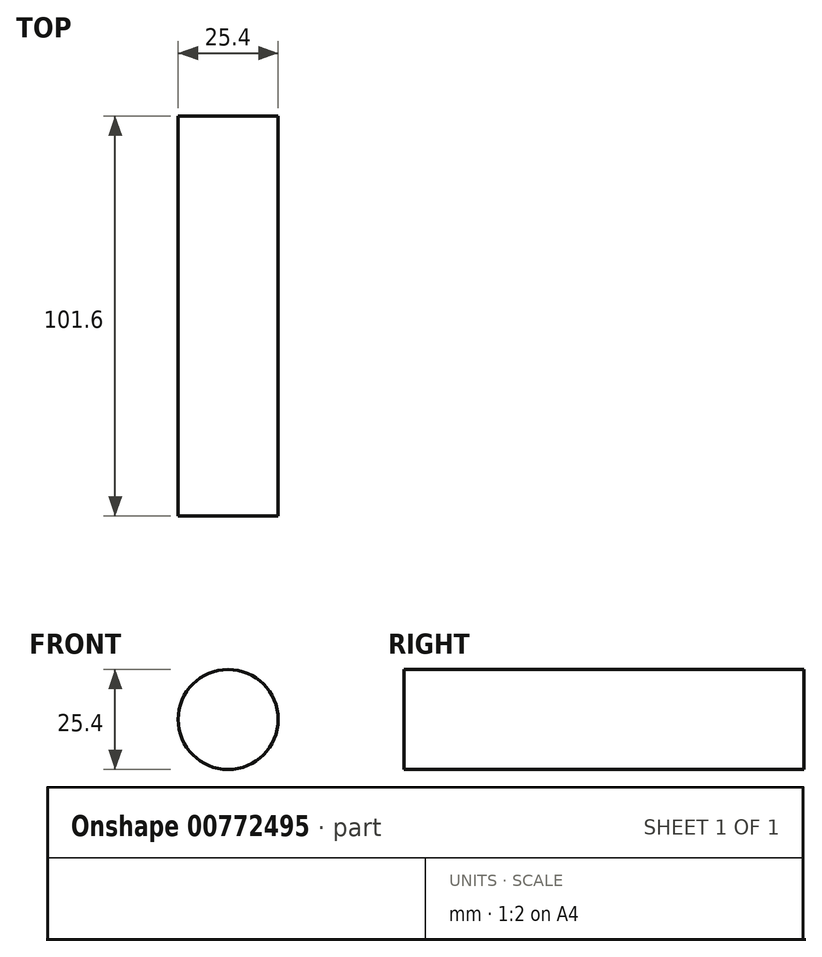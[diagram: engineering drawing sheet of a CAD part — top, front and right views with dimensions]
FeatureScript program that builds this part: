
annotation { "Feature Type Name" : "Feature", "Feature Type Description" : "" }
export const myFeature = defineFeature(function(context is Context, id is Id, definition is map)
    precondition{}
    {
        {
            var Q0;
            Q0=qCreatedBy(makeId("Front.planeOp"),FACE);
            var sketch = newSketch(context, id + "F0", { "sketchPlane" : qUnion([Q0])});
            skCircle(sketch, "E0", {"center": v(0, 0) * mm, "radius": 12.7 * mm});
            skSolve(sketch);
        }
        {
            var Q0;
            Q0=makeQuery(id+"F0.imprint","IMPRINT",FACE,{"disambiguationData":[TD([[makeQuery(id+"F0.imprint","IMPRINT",EDGE,{"derivedFrom":sQuery(id+"F0.wireOp",EDGE,"E0")}),1.0]])]});
            extrude(context, id + "F1", {"entities" : qUnion([Q0]), "oppositeDirection" : true, "depth" : 101.6 * mm, "offsetDistance" : 25.4 * mm});
        }
    });
